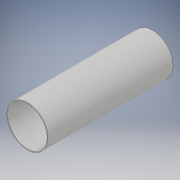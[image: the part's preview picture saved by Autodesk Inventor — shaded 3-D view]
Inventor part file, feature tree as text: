
AUTODESK INVENTOR PART (.ipt)
format: ipt  version: 2019 (Build 230136000, 136)  size: 99,328 bytes
history: native  units: mm
features: extrude x2, sketch x2
ambient origin geometry x8: Origin, YZ Plane, XZ Plane, XY Plane, X Axis, Y Axis, Z Axis, Center Point
bodies: Solid1 (feature_tree)
feature tree (4):
  extrude  "Extrusion1"  Depth=54.0mm TaperAngle=0.0deg
  extrude  "Extrusion2"  Depth=54.0mm TaperAngle=0.0deg
  sketch  "Sketch1"  dims[d0=17.72mm d1=54.0mm d2=0.0mm]
  sketch  "Sketch2"  dims[d3=17.03mm d4=54.0mm d5=0.0mm]
